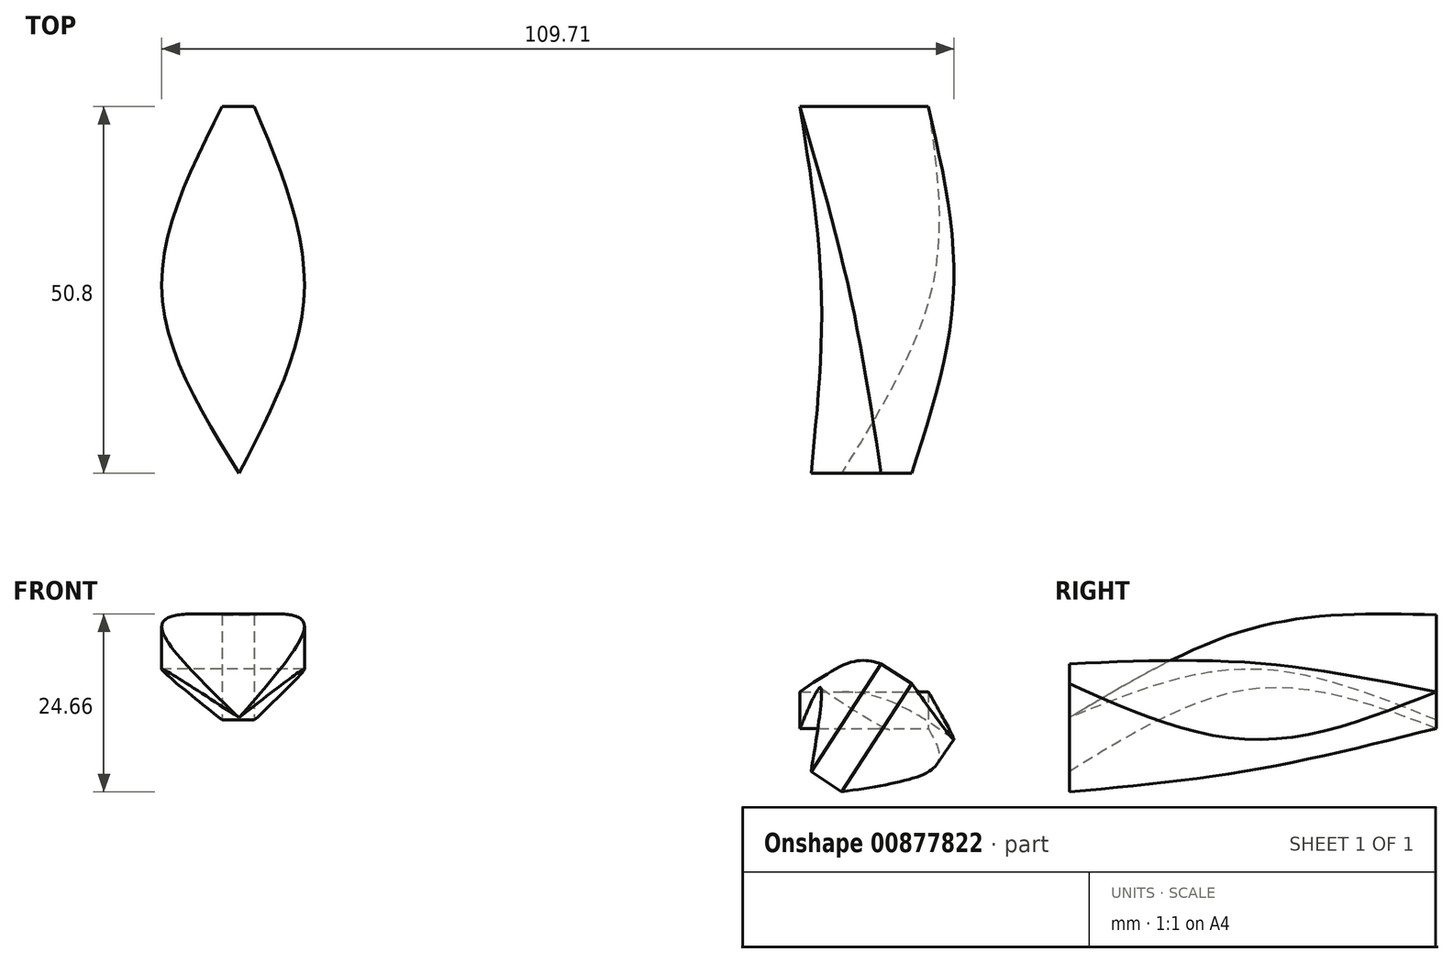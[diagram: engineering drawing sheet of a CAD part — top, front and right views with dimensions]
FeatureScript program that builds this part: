
annotation { "Feature Type Name" : "Feature", "Feature Type Description" : "" }
export const myFeature = defineFeature(function(context is Context, id is Id, definition is map)
    precondition{}
    {
        {
            var Q0;
            Q0=qCreatedBy(makeId("Front.planeOp"),FACE);
            cPlane(context, id + "F0", {"entities" : qUnion([Q0]), "cplaneType" : CPlaneType.OFFSET, "offset" : 25.4 * mm, "width" : 152.4 * mm, "height" : 152.4 * mm});
        }
        {
            var Q0;
            Q0=qCreatedBy(id+"F0.planeOp",FACE);
            cPlane(context, id + "F1", {"entities" : qUnion([Q0]), "cplaneType" : CPlaneType.OFFSET, "offset" : 25.4 * mm, "width" : 152.4 * mm, "height" : 152.4 * mm});
        }
        {
            var Q0;
            Q0=qCreatedBy(makeId("Front.planeOp"),FACE);
            var sketch = newSketch(context, id + "F2", { "sketchPlane" : qUnion([Q0])});
            skLineSegment(sketch, "E0.bottom", {"start": v(-54.48, 49.94) * mm, "end": v(-50.03, 49.94) * mm});
            skLineSegment(sketch, "E0.top", {"start": v(-54.48, 35.36) * mm, "end": v(-50.03, 35.36) * mm});
            skLineSegment(sketch, "E0.left", {"start": v(-54.48, 49.94) * mm, "end": v(-54.48, 35.36) * mm});
            skLineSegment(sketch, "E0.right", {"start": v(-50.03, 49.94) * mm, "end": v(-50.03, 35.36) * mm});
            skSolve(sketch);
        }
        {
            var Q0;
            Q0=qCreatedBy(id+"F0.planeOp",FACE);
            var sketch = newSketch(context, id + "F3", { "sketchPlane" : qUnion([Q0])});
            skLineSegment(sketch, "E1.bottom", {"start": v(-62.85, 48.1) * mm, "end": v(-43.12, 48.1) * mm});
            skLineSegment(sketch, "E1.top", {"start": v(-62.85, 42.4) * mm, "end": v(-43.12, 42.4) * mm});
            skLineSegment(sketch, "E1.left", {"start": v(-62.85, 48.1) * mm, "end": v(-62.85, 42.4) * mm});
            skLineSegment(sketch, "E1.right", {"start": v(-43.12, 48.1) * mm, "end": v(-43.12, 42.4) * mm});
            skSolve(sketch);
        }
        {
            var Q0;
            Q0=qCreatedBy(id+"F1.planeOp",FACE);
            var sketch = newSketch(context, id + "F4", { "sketchPlane" : qUnion([Q0])});
            skCircle(sketch, "E2.cCircle", {"center": v(-52.15, 35.7) * mm, "radius": 7.67 * mm, "construction": true});
            skLineSegment(sketch, "E2.0", {"start": v(-37.23, 39.28) * mm, "end": v(-56.5, 20.98) * mm});
            skLineSegment(sketch, "E2.1", {"start": v(-56.5, 20.98) * mm, "end": v(-62.71, 46.82) * mm});
            skLineSegment(sketch, "E2.2", {"start": v(-62.71, 46.82) * mm, "end": v(-37.23, 39.28) * mm});
            skPoint(sketch, "E2.0.midPoint", {"position": v(-46.87, 30.13) * mm});
            skSolve(sketch);
        }
        {
            var Q0;
            Q0=makeQuery(id+"F2.imprint","IMPRINT",FACE,{"disambiguationData":[TD([[makeQuery(id+"F2.imprint","IMPRINT",EDGE,{"derivedFrom":sQuery(id+"F2.wireOp",EDGE,"E0.bottom")}),-1.0]])]});
            var Q1;
            Q1=makeQuery(id+"F3.imprint","IMPRINT",FACE,{"disambiguationData":[TD([[makeQuery(id+"F3.imprint","IMPRINT",EDGE,{"derivedFrom":sQuery(id+"F3.wireOp",EDGE,"E1.bottom")}),-1.0]])]});
            var Q2;
            Q2=sQuery(id+"F4.wireOp",VERTEX,"E2.cCircle.center");
            loft(context, id + "F5", {"sheetProfilesArray" : [{ "sheetProfileEntities" : qUnion([Q0]) }, { "sheetProfileEntities" : qUnion([Q1]) }, { "sheetProfileEntities" : qUnion([Q2]) }]});
        }
        {
            var Q0;
            Q0=qCreatedBy(makeId("Front.planeOp"),FACE);
            var sketch = newSketch(context, id + "F6", { "sketchPlane" : qUnion([Q0])});
            skLineSegment(sketch, "E3.bottom", {"start": v(25.51, 39.28) * mm, "end": v(43.3, 39.28) * mm});
            skLineSegment(sketch, "E3.top", {"start": v(25.51, 34.2) * mm, "end": v(43.3, 34.2) * mm});
            skLineSegment(sketch, "E3.left", {"start": v(25.51, 39.28) * mm, "end": v(25.51, 34.2) * mm});
            skLineSegment(sketch, "E3.right", {"start": v(43.3, 39.28) * mm, "end": v(43.3, 34.2) * mm});
            skSolve(sketch);
        }
        {
            var Q0;
            Q0=qCreatedBy(id+"F0.planeOp",FACE);
            var sketch = newSketch(context, id + "F7", { "sketchPlane" : qUnion([Q0])});
            skPoint(sketch, "E4.middle", {"position": v(33.7, 21.4) * mm});
            skPoint(sketch, "E4.middle.positionSnap0", {"position": v(27.11, 21.4) * mm});
            skPoint(sketch, "E4.centerSnap0", {"position": v(27.11, 21.4) * mm});
            skPoint(sketch, "E5.orphan", {"position": v(27.11, 18.6) * mm});
            skPoint(sketch, "E6.left.end.orphan", {"position": v(27.11, 24.18) * mm});
            skPoint(sketch, "E4.right.end.orphan", {"position": v(24.64, 23.97) * mm});
            skPoint(sketch, "E4.right.start.orphan", {"position": v(24.64, 18.81) * mm});
            skPoint(sketch, "E4.left.end.orphan", {"position": v(42.78, 23.97) * mm});
            skPoint(sketch, "E4.left.start.orphan", {"position": v(42.78, 18.81) * mm});
            skLineSegment(sketch, "E7", {"start": v(32.31, 43.28) * mm, "end": v(46.8, 32.65) * mm});
            skLineSegment(sketch, "E8", {"start": v(46.8, 32.65) * mm, "end": v(43.73, 28.46) * mm});
            skLineSegment(sketch, "E9", {"start": v(43.73, 28.46) * mm, "end": v(28.47, 39.66) * mm});
            skLineSegment(sketch, "E10", {"start": v(28.47, 39.66) * mm, "end": v(32.31, 43.28) * mm});
            skSolve(sketch);
        }
        {
            var Q0;
            Q0=qCreatedBy(id+"F1.planeOp",FACE);
            var sketch = newSketch(context, id + "F8", { "sketchPlane" : qUnion([Q0])});
            skPoint(sketch, "E11.end.orphan", {"position": v(43.56, 40.38) * mm});
            skPoint(sketch, "E12.end.orphan", {"position": v(43.56, 39.53) * mm});
            skLineSegment(sketch, "E13", {"start": v(36.76, 43.14) * mm, "end": v(41.01, 40.38) * mm});
            skLineSegment(sketch, "E14", {"start": v(41.01, 40.38) * mm, "end": v(31.28, 25.4) * mm});
            skLineSegment(sketch, "E15", {"start": v(36.76, 43.14) * mm, "end": v(27.07, 28.22) * mm});
            skLineSegment(sketch, "E16", {"start": v(27.07, 28.22) * mm, "end": v(31.28, 25.4) * mm});
            skSolve(sketch);
        }
        {
            var Q0;
            Q0=makeQuery(id+"F6.imprint","IMPRINT",FACE,{"disambiguationData":[TD([[makeQuery(id+"F6.imprint","IMPRINT",EDGE,{"derivedFrom":sQuery(id+"F6.wireOp",EDGE,"E3.bottom")}),-1.0]])]});
            var Q1;
            Q1=makeQuery(id+"F7.imprint","IMPRINT",FACE,{"disambiguationData":[TD([[makeQuery(id+"F7.imprint","IMPRINT",EDGE,{"derivedFrom":sQuery(id+"F7.wireOp",EDGE,"E7")}),-1.0]])]});
            var Q2;
            Q2=makeQuery(id+"F8.imprint","IMPRINT",FACE,{"disambiguationData":[TD([[makeQuery(id+"F8.imprint","IMPRINT",EDGE,{"derivedFrom":sQuery(id+"F8.wireOp",EDGE,"E13")}),-1.0]])]});
            loft(context, id + "F9", {"sheetProfilesArray" : [{ "sheetProfileEntities" : qUnion([Q0]) }, { "sheetProfileEntities" : qUnion([Q1]) }, { "sheetProfileEntities" : qUnion([Q2]) }]});
        }
    });
